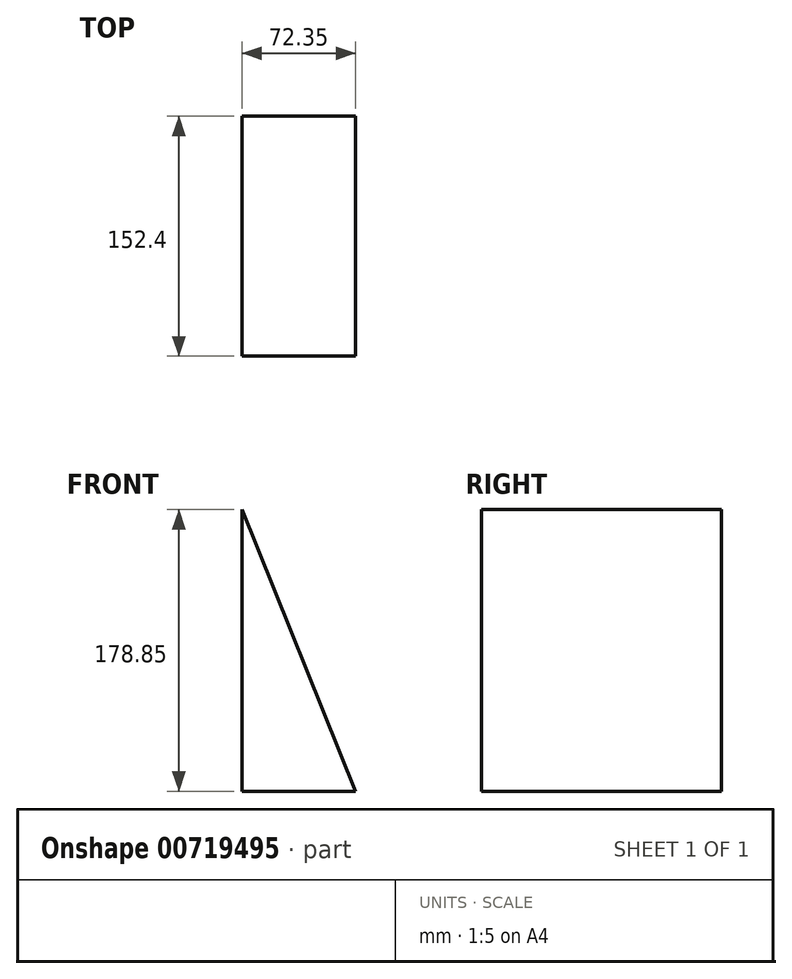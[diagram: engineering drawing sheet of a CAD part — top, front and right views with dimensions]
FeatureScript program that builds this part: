
annotation { "Feature Type Name" : "Feature", "Feature Type Description" : "" }
export const myFeature = defineFeature(function(context is Context, id is Id, definition is map)
    precondition{}
    {
        {
            var Q0;
            Q0=qCreatedBy(makeId("Front.planeOp"),FACE);
            var sketch = newSketch(context, id + "F0", { "sketchPlane" : qUnion([Q0])});
            skLineSegment(sketch, "E0", {"start": v(0, 0) * mm, "end": v(0, 188.37) * mm});
            skLineSegment(sketch, "E1", {"start": v(0, 188.37) * mm, "end": v(25.4, 188.37) * mm});
            skLineSegment(sketch, "E2", {"start": v(25.4, 188.37) * mm, "end": v(101.6, 0) * mm});
            skLineSegment(sketch, "E3", {"start": v(101.6, 0) * mm, "end": v(0, 0) * mm});
            skLineSegment(sketch, "E4", {"start": v(101.6, 0) * mm, "end": v(78.05, -9.53) * mm});
            skLineSegment(sketch, "E5", {"start": v(78.05, -9.53) * mm, "end": v(1.85, 178.85) * mm});
            skLineSegment(sketch, "E6", {"start": v(1.85, 178.85) * mm, "end": v(25.4, 188.37) * mm});
            skLineSegment(sketch, "E7", {"start": v(101.6, 0) * mm, "end": v(101.6, 178.28) * mm, "construction": true});
            skLineSegment(sketch, "E8", {"start": v(1.85, 178.85) * mm, "end": v(29.25, 178.85) * mm});
            skLineSegment(sketch, "E9", {"start": v(1.85, 178.85) * mm, "end": v(1.85, 0) * mm});
            skLineSegment(sketch, "E10", {"start": v(1.85, 0) * mm, "end": v(74.2, 0) * mm});
            skPoint(sketch, "E11.endSnap0", {"position": v(38.03, 0) * mm});
            skSolve(sketch);
        }
        {
            var Q0;
            {var subQ0=sQuery(id+"F0.wireOp",EDGE,"E9");Q0=makeQuery(id+"F0.imprint","IMPRINT",FACE,{"disambiguationData":[TD([[makeQuery(id+"F0.imprint","IMPRINT",EDGE,{"derivedFrom":subQ0}),1.0]])]});}
            extrude(context, id + "F1", {"entities" : qUnion([Q0]), "depth" : 152.4 * mm, "offsetDistance" : 25.4 * mm});
        }
    });
